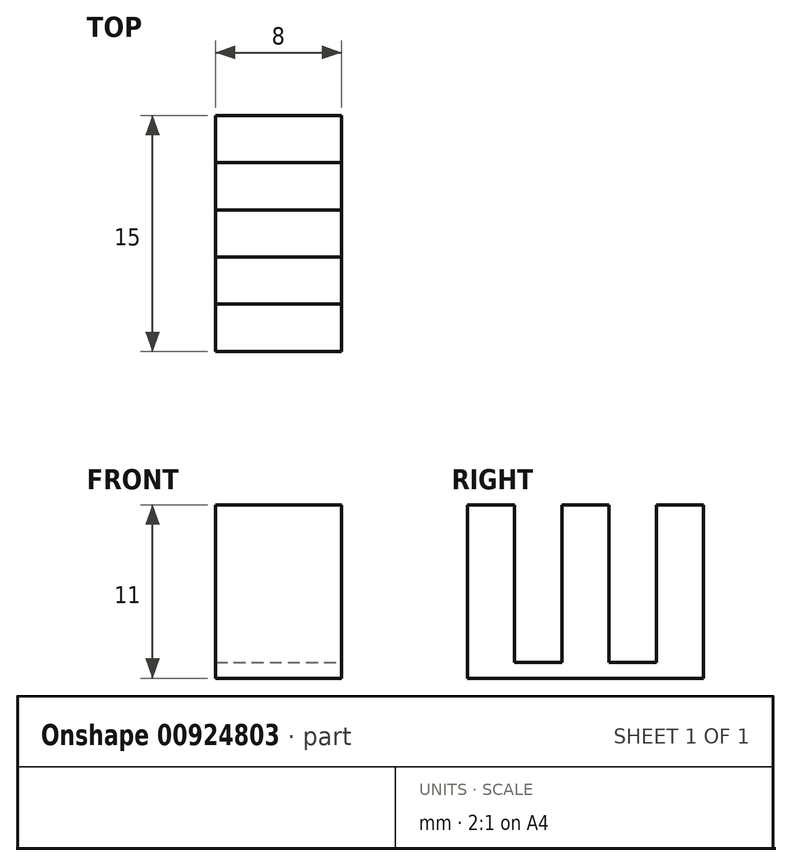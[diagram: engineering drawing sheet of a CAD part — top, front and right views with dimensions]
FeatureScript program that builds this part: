
annotation { "Feature Type Name" : "Feature", "Feature Type Description" : "" }
export const myFeature = defineFeature(function(context is Context, id is Id, definition is map)
    precondition{}
    {
        {
            var Q0;
            Q0=qCreatedBy(makeId("Top.planeOp"),FACE);
            var sketch = newSketch(context, id + "F0", { "sketchPlane" : qUnion([Q0])});
            skLineSegment(sketch, "E0.bottom", {"start": v(-4, 11) * mm, "end": v(4, 11) * mm});
            skLineSegment(sketch, "E0.top", {"start": v(-4, -4) * mm, "end": v(4, -4) * mm});
            skLineSegment(sketch, "E0.left", {"start": v(-4, 11) * mm, "end": v(-4, -4) * mm});
            skLineSegment(sketch, "E0.right", {"start": v(4, 11) * mm, "end": v(4, -4) * mm});
            skLineSegment(sketch, "E1.top", {"start": v(-4, 8) * mm, "end": v(4, 8) * mm});
            skLineSegment(sketch, "E1.left", {"start": v(-4, 11) * mm, "end": v(-4, 8) * mm});
            skLineSegment(sketch, "E1.right", {"start": v(4, 11) * mm, "end": v(4, 8) * mm});
            skLineSegment(sketch, "E2", {"start": v(-4, -1) * mm, "end": v(4, -1) * mm});
            skLineSegment(sketch, "E3", {"start": v(-4, 2) * mm, "end": v(4, 2) * mm});
            skLineSegment(sketch, "E4", {"start": v(4, 2) * mm, "end": v(4, 5) * mm});
            skLineSegment(sketch, "E5", {"start": v(4, 5) * mm, "end": v(-4, 5) * mm});
            skSolve(sketch);
        }
        {
            var Q0;
            {var subQ3=sQuery(id+"F0.wireOp",EDGE,"E1.top");var subQ9=makeQuery(id+"F0.imprint","IMPRINT",EDGE,{"derivedFrom":subQ3});var subQ10=sQuery(id+"F0.wireOp",EDGE,"E0.top");var subQ11=sQuery(id+"F0.wireOp",EDGE,"E0.bottom");Q0=qUnion([makeQuery(id+"F0.imprint","IMPRINT",FACE,{"disambiguationData":[TD([[makeQuery(id+"F0.imprint","IMPRINT",EDGE,{"derivedFrom":subQ11}),-1.0]])]}),makeQuery(id+"F0.imprint","IMPRINT",FACE,{"disambiguationData":[TD([[makeQuery(id+"F0.imprint","IMPRINT",EDGE,{"derivedFrom":subQ10}),1.0]])]}),makeQuery(id+"F0.imprint","IMPRINT",FACE,{"disambiguationData":[TD([[subQ9,-1.0]])]})]);}
            var Q1;
            {var subQ0=sQuery(id+"F0.wireOp",EDGE,"E3");Q1=makeQuery(id+"F0.imprint","IMPRINT",FACE,{"disambiguationData":[TD([[makeQuery(id+"F0.imprint","IMPRINT",EDGE,{"derivedFrom":subQ0}),1.0]])]});}
            var Q2;
            {var subQ0=sQuery(id+"F0.wireOp",EDGE,"E2");Q2=makeQuery(id+"F0.imprint","IMPRINT",FACE,{"disambiguationData":[TD([[makeQuery(id+"F0.imprint","IMPRINT",EDGE,{"derivedFrom":subQ0}),1.0]])]});}
            extrude(context, id + "F1", {"entities" : qUnion([Q0, Q1, Q2]), "depth" : 1 * mm, "offsetDistance" : 25 * mm});
        }
        {
            var Q0;
            {var subQ0=sQuery(id+"F0.wireOp",EDGE,"E0.top");Q0=makeQuery(id+"F0.imprint","IMPRINT",FACE,{"disambiguationData":[TD([[makeQuery(id+"F0.imprint","IMPRINT",EDGE,{"derivedFrom":subQ0}),1.0]])]});}
            var Q1;
            {var subQ0=sQuery(id+"F0.wireOp",EDGE,"E0.bottom");Q1=makeQuery(id+"F0.imprint","IMPRINT",FACE,{"disambiguationData":[TD([[makeQuery(id+"F0.imprint","IMPRINT",EDGE,{"derivedFrom":subQ0}),-1.0]])]});}
            var Q2;
            {var subQ0=sQuery(id+"F0.wireOp",EDGE,"E3");Q2=makeQuery(id+"F0.imprint","IMPRINT",FACE,{"disambiguationData":[TD([[makeQuery(id+"F0.imprint","IMPRINT",EDGE,{"derivedFrom":subQ0}),1.0]])]});}
            extrude(context, id + "F2", {"entities" : qUnion([Q0, Q1, Q2]), "operationType" : NewBodyOperationType.ADD, "depth" : 11 * mm, "offsetDistance" : 25 * mm});
        }
    });
